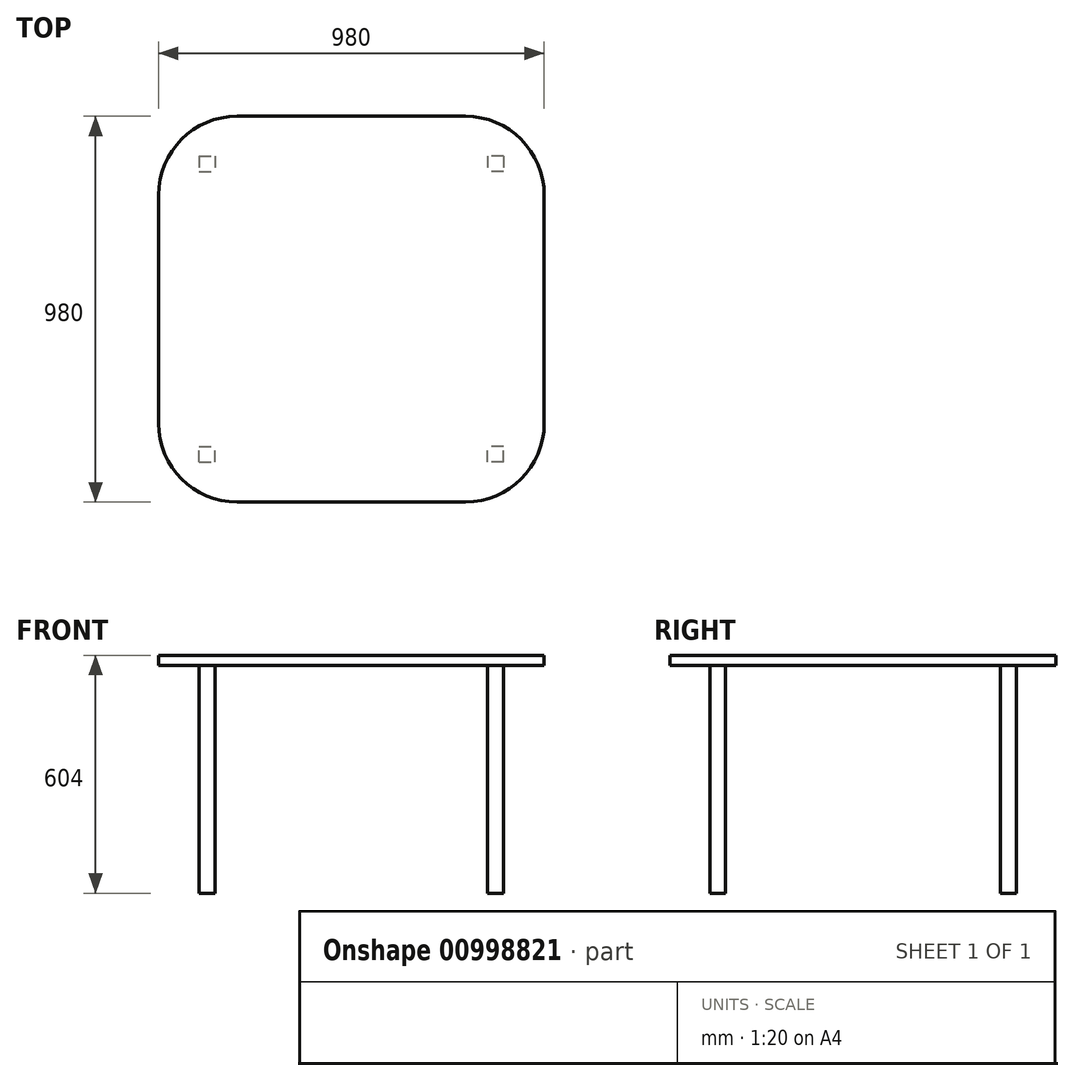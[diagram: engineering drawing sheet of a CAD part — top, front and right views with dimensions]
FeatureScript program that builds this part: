
annotation { "Feature Type Name" : "Feature", "Feature Type Description" : "" }
export const myFeature = defineFeature(function(context is Context, id is Id, definition is map)
    precondition{}
    {
        {
            var Q0;
            Q0=qCreatedBy(makeId("Top.planeOp"),FACE);
            var sketch = newSketch(context, id + "F0", { "sketchPlane" : qUnion([Q0])});
            skLineSegment(sketch, "E0.bottom", {"start": v(200, 0) * mm, "end": v(780, 0) * mm});
            skLineSegment(sketch, "E0.top", {"start": v(200, 980) * mm, "end": v(780, 980) * mm});
            skLineSegment(sketch, "E0.left", {"start": v(0, 200) * mm, "end": v(0, 780) * mm});
            skLineSegment(sketch, "E0.right", {"start": v(980, 200) * mm, "end": v(980, 780) * mm});
            skPoint(sketch, "E1.visualSharp", {"position": v(980, 980) * mm});
            skArc(sketch, "E1.filletArc", {"start": v(980, 780) * mm, "mid": v(921.42, 921.42) * mm, "end": v(780, 980) * mm});
            skPoint(sketch, "E2.visualSharp", {"position": v(0, 980) * mm});
            skArc(sketch, "E2.filletArc", {"start": v(200, 980) * mm, "mid": v(58.58, 921.42) * mm, "end": v(0, 780) * mm});
            skPoint(sketch, "E3.visualSharp", {"position": v(0, 0) * mm});
            skArc(sketch, "E3.filletArc", {"start": v(0, 200) * mm, "mid": v(58.58, 58.58) * mm, "end": v(200, 0) * mm});
            skPoint(sketch, "E4.visualSharp", {"position": v(980, 0) * mm});
            skArc(sketch, "E4.filletArc", {"start": v(780, 0) * mm, "mid": v(921.42, 58.58) * mm, "end": v(980, 200) * mm});
            skSolve(sketch);
        }
        {
            var Q0;
            Q0 = qSketchRegion(id + "F0", true);
            extrude(context, id + "F1", {"entities" : qUnion([Q0]), "depth" : 25 * mm, "offsetDistance" : 25 * mm});
        }
        {
            var Q0;
            Q0=makeQuery(id+"F1.opExtrude","CAP_FACE",FACE,{"disambiguationData":[OSD([sQuery(id+"F0.wireOp",EDGE,"E0.bottom"),sQuery(id+"F0.wireOp",EDGE,"E0.top"),sQuery(id+"F0.wireOp",EDGE,"E0.left"),sQuery(id+"F0.wireOp",EDGE,"E0.right"),sQuery(id+"F0.wireOp",EDGE,"E1.filletArc"),sQuery(id+"F0.wireOp",EDGE,"E2.filletArc"),sQuery(id+"F0.wireOp",EDGE,"E3.filletArc"),sQuery(id+"F0.wireOp",EDGE,"E4.filletArc")])],"isStart":true});
            var sketch = newSketch(context, id + "F2", { "sketchPlane" : qUnion([Q0])});
            skLineSegment(sketch, "E5.bottom", {"start": v(103.72, -101) * mm, "end": v(143.72, -101) * mm});
            skLineSegment(sketch, "E5.top", {"start": v(103.72, -141) * mm, "end": v(143.72, -141) * mm});
            skLineSegment(sketch, "E5.left", {"start": v(103.72, -101) * mm, "end": v(103.72, -141) * mm});
            skLineSegment(sketch, "E5.right", {"start": v(143.72, -101) * mm, "end": v(143.72, -141) * mm});
            skLineSegment(sketch, "E6", {"start": v(490, 0) * mm, "end": v(490, -980) * mm, "construction": true});
            skLineSegment(sketch, "E7", {"start": v(0, -490) * mm, "end": v(980, -490) * mm, "construction": true});
            skLineSegment(sketch, "E8.MirrorCS", {"start": v(876.28, -101) * mm, "end": v(876.28, -141) * mm});
            skLineSegment(sketch, "E9.MirrorCS", {"start": v(836.28, -101) * mm, "end": v(836.28, -141) * mm});
            skLineSegment(sketch, "E10.MirrorCS", {"start": v(876.28, -101) * mm, "end": v(836.28, -101) * mm});
            skLineSegment(sketch, "E11.MirrorCS", {"start": v(876.28, -141) * mm, "end": v(836.28, -141) * mm});
            skLineSegment(sketch, "E12.MirrorCS", {"start": v(980, -490) * mm, "end": v(0, -490) * mm, "construction": true});
            skLineSegment(sketch, "E13.MirrorCS", {"start": v(103.72, -839) * mm, "end": v(143.72, -839) * mm});
            skLineSegment(sketch, "E14.MirrorCS", {"start": v(143.72, -879) * mm, "end": v(143.72, -839) * mm});
            skLineSegment(sketch, "E15.MirrorCS", {"start": v(103.72, -879) * mm, "end": v(143.72, -879) * mm});
            skLineSegment(sketch, "E16.MirrorCS", {"start": v(103.72, -879) * mm, "end": v(103.72, -839) * mm});
            skLineSegment(sketch, "E17.MirrorCS", {"start": v(876.28, -879) * mm, "end": v(876.28, -839) * mm});
            skLineSegment(sketch, "E18.MirrorCS", {"start": v(836.28, -879) * mm, "end": v(836.28, -839) * mm});
            skLineSegment(sketch, "E19.MirrorCS", {"start": v(876.28, -879) * mm, "end": v(836.28, -879) * mm});
            skLineSegment(sketch, "E20.MirrorCS", {"start": v(876.28, -839) * mm, "end": v(836.28, -839) * mm});
            skSolve(sketch);
        }
        {
            var Q0;
            Q0 = qSketchRegion(id + "F2", true);
            extrude(context, id + "F3", {"entities" : qUnion([Q0]), "operationType" : NewBodyOperationType.ADD, "depth" : 579 * mm, "offsetDistance" : 25 * mm});
        }
    });
